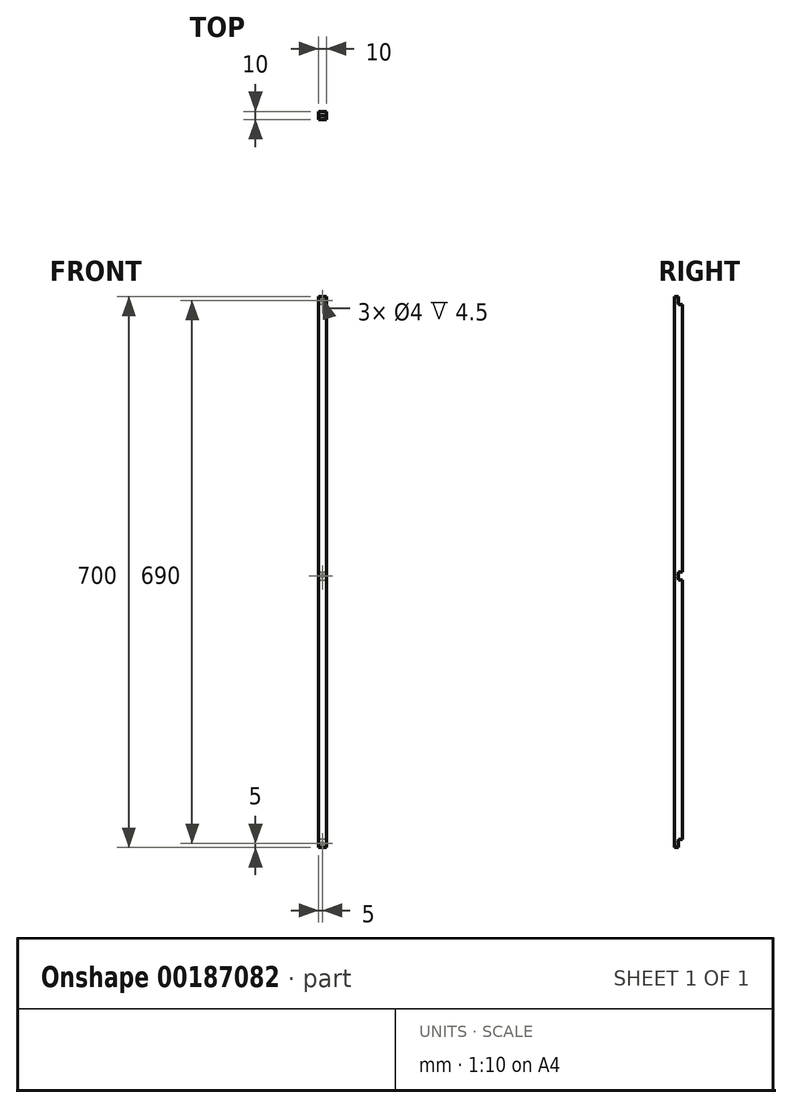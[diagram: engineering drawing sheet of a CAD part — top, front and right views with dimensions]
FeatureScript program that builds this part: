
annotation { "Feature Type Name" : "Feature", "Feature Type Description" : "" }
export const myFeature = defineFeature(function(context is Context, id is Id, definition is map)
    precondition{}
    {
        {
            var Q0;
            Q0=qCreatedBy(makeId("Right.planeOp"),FACE);
            var sketch = newSketch(context, id + "F0", { "sketchPlane" : qUnion([Q0])});
            skLineSegment(sketch, "E0", {"start": v(0, 0) * mm, "end": v(0, 340) * mm});
            skLineSegment(sketch, "E1", {"start": v(0, 340) * mm, "end": v(-5, 340) * mm});
            skLineSegment(sketch, "E2", {"start": v(-5, 340) * mm, "end": v(-5, 350) * mm});
            skLineSegment(sketch, "E3", {"start": v(-5, 350) * mm, "end": v(-10, 350) * mm});
            skLineSegment(sketch, "E4", {"start": v(-10, 350) * mm, "end": v(-10, 0) * mm});
            skLineSegment(sketch, "E5", {"start": v(-10, 0) * mm, "end": v(0, 0) * mm});
            skSolve(sketch);
        }
        {
            var Q0;
            Q0=qSketchRegion(id+"F0",true);
            extrude(context, id + "F1", {"entities" : qUnion([Q0]), "depth" : 10 * mm});
        }
        {
            var Q0;
            Q0=makeQuery(id+"F1.opExtrude","SWEPT_FACE",FACE,{"disambiguationData":[OSD([sQuery(id+"F0.wireOp",EDGE,"E2")])]});
            var sketch = newSketch(context, id + "F2", { "sketchPlane" : qUnion([Q0])});
            skCircle(sketch, "E6", {"center": v(-5, 345) * mm, "radius": 2 * mm});
            skPoint(sketch, "E6.centerSnap0", {"position": v(-5, 350) * mm});
            skPoint(sketch, "E6.centerSnap1", {"position": v(0, 345) * mm});
            skSolve(sketch);
        }
        {
            var Q0;
            Q0=qSketchRegion(id+"F2",true);
            extrude(context, id + "F3", {"entities" : qUnion([Q0]), "operationType" : NewBodyOperationType.REMOVE, "oppositeDirection" : true, "depth" : 4.5 * mm});
        }
        {
            var Q0;
            Q0=makeQuery(id+"F1.opExtrude","SWEPT_BODY",BODY,{"disambiguationData":[OSD([sQuery(id+"F0.wireOp",EDGE,"E0"),sQuery(id+"F0.wireOp",EDGE,"E1"),sQuery(id+"F0.wireOp",EDGE,"E2"),sQuery(id+"F0.wireOp",EDGE,"E3"),sQuery(id+"F0.wireOp",EDGE,"E4"),sQuery(id+"F0.wireOp",EDGE,"E5")])]});
            var Q1;
            Q1=qCreatedBy(makeId("Top.planeOp"),FACE);
            mirror(context, id + "F4", {"operationType" : NewBodyOperationType.ADD, "entities" : qUnion([Q0]), "mirrorPlane" : qUnion([Q1])});
        }
        {
            var Q0;
            {var subQ0=makeQuery(id+"F1.opExtrude","CAP_FACE",FACE,{"disambiguationData":[OSD([sQuery(id+"F0.wireOp",EDGE,"E0"),sQuery(id+"F0.wireOp",EDGE,"E1"),sQuery(id+"F0.wireOp",EDGE,"E2"),sQuery(id+"F0.wireOp",EDGE,"E3"),sQuery(id+"F0.wireOp",EDGE,"E4"),sQuery(id+"F0.wireOp",EDGE,"E5")])],"isStart":false});Q0=makeQuery(id+"F4.boolean.opBoolean","MERGE",FACE,{"derivedFrom":[subQ0,makeQuery(id+"F4.opPattern","COPY",FACE,{"derivedFrom":subQ0,"instanceName":"1"})]});}
            var sketch = newSketch(context, id + "F5", { "sketchPlane" : qUnion([Q0])});
            skLineSegment(sketch, "E7.bottom", {"start": v(0, 0) * mm, "end": v(-5, 0) * mm});
            skLineSegment(sketch, "E7.top", {"start": v(0, -10) * mm, "end": v(-5, -10) * mm});
            skLineSegment(sketch, "E7.left", {"start": v(0, 0) * mm, "end": v(0, -10) * mm});
            skLineSegment(sketch, "E7.right", {"start": v(-5, 0) * mm, "end": v(-5, -10) * mm});
            skSolve(sketch);
        }
        {
            var Q0;
            Q0=qSketchRegion(id+"F5",true);
            extrude(context, id + "F6", {"entities" : qUnion([Q0]), "operationType" : NewBodyOperationType.REMOVE, "endBound" : BoundingType.THROUGH_ALL, "oppositeDirection" : true, "depth" : 25 * mm});
        }
        {
            var Q0;
            Q0=makeQuery(id+"F6.boolean.opBoolean","COPY",FACE,{"derivedFrom":makeQuery(id+"F6.opExtrude","SWEPT_FACE",FACE,{"disambiguationData":[OSD([sQuery(id+"F5.wireOp",EDGE,"E7.right")])]})});
            var sketch = newSketch(context, id + "F7", { "sketchPlane" : qUnion([Q0])});
            skCircle(sketch, "E8", {"center": v(-5, -5) * mm, "radius": 2 * mm});
            skPoint(sketch, "E8.centerSnap0", {"position": v(0, -5) * mm});
            skPoint(sketch, "E8.centerSnap1", {"position": v(-5, 0) * mm});
            skSolve(sketch);
        }
        {
            var Q0;
            Q0=qSketchRegion(id+"F7",true);
            extrude(context, id + "F8", {"entities" : qUnion([Q0]), "operationType" : NewBodyOperationType.REMOVE, "oppositeDirection" : true, "depth" : 4.5 * mm});
        }
    });
